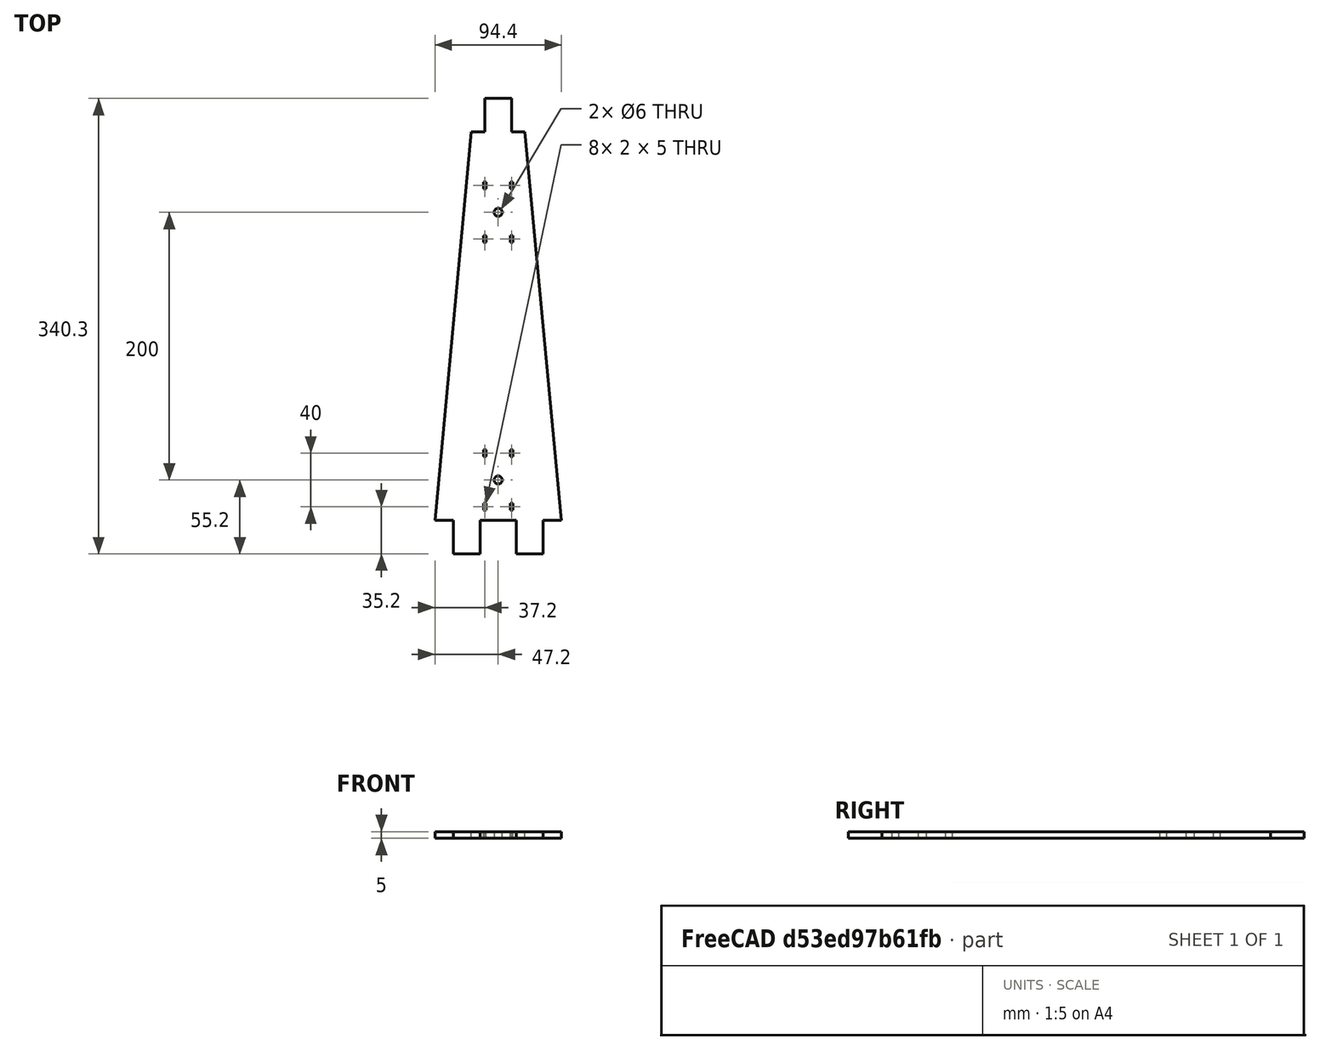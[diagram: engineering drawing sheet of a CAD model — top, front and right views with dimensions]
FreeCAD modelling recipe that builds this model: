
FCSTD DOCUMENT  (FreeCAD 0.16R6712 (Git))
Label: Vertical
License: All rights reserved
LicenseURL: http://en.wikipedia.org/wiki/All_rights_reserved
objects: Sketcher::SketchObject×1, PartDesign::Pad×1
note: 3 computed .brp shape members not serialized (recipe doc carries the construction recipe); baked Part::Feature solids carry a one-line shape summary decoded from their .brp

FEATURE [Sketcher::SketchObject] Sketch010
  sketch-geometry (67):
    g0: LineSegment StartX=-10 StartY=160.1 StartZ=0 EndX=-20 EndY=160.1 EndZ=0
    g1: LineSegment StartX=-20 StartY=160.1 StartZ=0 EndX=-47.2 EndY=-130.1 EndZ=0
    g2: LineSegment StartX=-47.2 StartY=-130.1 StartZ=0 EndX=-33.6 EndY=-130.1 EndZ=0
    g3: LineSegment StartX=-33.6 StartY=-130.1 StartZ=0 EndX=-33.6 EndY=-155.2 EndZ=0
    g4: LineSegment StartX=-33.6 StartY=-155.2 StartZ=0 EndX=-13.4 EndY=-155.2 EndZ=0
    g5: LineSegment StartX=-13.4 StartY=-155.2 StartZ=0 EndX=-13.4 EndY=-130.1 EndZ=0
    g6: LineSegment StartX=-13.4 StartY=-130.1 StartZ=0 EndX=13.4 EndY=-130.1 EndZ=0
    g7: LineSegment StartX=13.4 StartY=-130.1 StartZ=0 EndX=13.4 EndY=-155.2 EndZ=0
    g8: LineSegment StartX=13.4 StartY=-155.2 StartZ=0 EndX=33.6 EndY=-155.2 EndZ=0
    g9: LineSegment StartX=33.6 StartY=-155.2 StartZ=0 EndX=33.6 EndY=-130.1 EndZ=0
    g10: LineSegment StartX=33.6 StartY=-130.1 StartZ=0 EndX=47.2 EndY=-130.1 EndZ=0
    g11: LineSegment StartX=47.2 StartY=-130.1 StartZ=0 EndX=20 EndY=160.1 EndZ=0
    g12: LineSegment StartX=20 StartY=160.1 StartZ=0 EndX=10 EndY=160.1 EndZ=0
    g13: LineSegment StartX=10 StartY=160.1 StartZ=0 EndX=10 EndY=185.1 EndZ=0
    g14: LineSegment StartX=10 StartY=185.1 StartZ=0 EndX=-10 EndY=185.1 EndZ=0
    g15: LineSegment StartX=-10 StartY=185.1 StartZ=0 EndX=-10 EndY=160.1 EndZ=0
    g16: LineSegment [constr] StartX=-140 StartY=-130.1 StartZ=0 EndX=140 EndY=-130.1 EndZ=0
    g17: LineSegment [constr] StartX=-140 StartY=-155.2 StartZ=0 EndX=140 EndY=-155.2 EndZ=0
    g18: LineSegment [constr] StartX=-140 StartY=-100 StartZ=0 EndX=140 EndY=-100 EndZ=0
    g19: Circle CenterX=0 CenterY=-100 CenterZ=0 NormalX=0 NormalY=0 NormalZ=1 Radius=3
    g20: LineSegment [constr] StartX=-140 StartY=100 StartZ=0 EndX=140 EndY=100 EndZ=0
    g21: Circle CenterX=0 CenterY=100 CenterZ=0 NormalX=0 NormalY=0 NormalZ=1 Radius=3
    g22: LineSegment [constr] StartX=-31 StartY=19.5 StartZ=0 EndX=31 EndY=19.5 EndZ=0
    g23: LineSegment [constr] StartX=-15 StartY=-75 StartZ=0 EndX=15 EndY=-75 EndZ=0
    g24: LineSegment [constr] StartX=15 StartY=-75 StartZ=0 EndX=15 EndY=-125 EndZ=0
    g25: LineSegment [constr] StartX=15 StartY=-125 StartZ=0 EndX=-15 EndY=-125 EndZ=0
    g26: LineSegment [constr] StartX=-15 StartY=-125 StartZ=0 EndX=-15 EndY=-75 EndZ=0
    g27: LineSegment [constr] StartX=-15 StartY=125 StartZ=0 EndX=15 EndY=125 EndZ=0
    g28: LineSegment [constr] StartX=15 StartY=125 StartZ=0 EndX=15 EndY=75 EndZ=0
    g29: LineSegment [constr] StartX=15 StartY=75 StartZ=0 EndX=-15 EndY=75 EndZ=0
    g30: LineSegment [constr] StartX=-15 StartY=75 StartZ=0 EndX=-15 EndY=125 EndZ=0
    g31: LineSegment StartX=-11 StartY=-77.5 StartZ=0 EndX=-9 EndY=-77.5 EndZ=0
    g32: LineSegment StartX=-9 StartY=-77.5 StartZ=0 EndX=-9 EndY=-82.5 EndZ=0
    g33: LineSegment StartX=-9 StartY=-82.5 StartZ=0 EndX=-11 EndY=-82.5 EndZ=0
    g34: LineSegment StartX=-11 StartY=-82.5 StartZ=0 EndX=-11 EndY=-77.5 EndZ=0
    g35: LineSegment StartX=9 StartY=-77.5 StartZ=0 EndX=11 EndY=-77.5 EndZ=0
    g36: LineSegment StartX=11 StartY=-77.5 StartZ=0 EndX=11 EndY=-82.5 EndZ=0
    g37: LineSegment StartX=11 StartY=-82.5 StartZ=0 EndX=9 EndY=-82.5 EndZ=0
    g38: LineSegment StartX=9 StartY=-82.5 StartZ=0 EndX=9 EndY=-77.5 EndZ=0
    g39: LineSegment StartX=-11 StartY=-117.5 StartZ=0 EndX=-9 EndY=-117.5 EndZ=0
    g40: LineSegment StartX=-9 StartY=-117.5 StartZ=0 EndX=-9 EndY=-122.5 EndZ=0
    g41: LineSegment StartX=-9 StartY=-122.5 StartZ=0 EndX=-11 EndY=-122.5 EndZ=0
    g42: LineSegment StartX=-11 StartY=-122.5 StartZ=0 EndX=-11 EndY=-117.5 EndZ=0
    g43: LineSegment StartX=9 StartY=-117.5 StartZ=0 EndX=11 EndY=-117.5 EndZ=0
    g44: LineSegment StartX=11 StartY=-117.5 StartZ=0 EndX=11 EndY=-122.5 EndZ=0
    g45: LineSegment StartX=11 StartY=-122.5 StartZ=0 EndX=9 EndY=-122.5 EndZ=0
    g46: LineSegment StartX=9 StartY=-122.5 StartZ=0 EndX=9 EndY=-117.5 EndZ=0
    g47: LineSegment [constr] StartX=-10 StartY=-130.1 StartZ=0 EndX=-10 EndY=185.1 EndZ=0
    g48: LineSegment [constr] StartX=10 StartY=185.1 StartZ=0 EndX=10 EndY=-130.1 EndZ=0
    g49: LineSegment StartX=-11 StartY=122.5 StartZ=0 EndX=-9 EndY=122.5 EndZ=0
    g50: LineSegment StartX=-9 StartY=122.5 StartZ=0 EndX=-9 EndY=117.5 EndZ=0
    g51: LineSegment StartX=-9 StartY=117.5 StartZ=0 EndX=-11 EndY=117.5 EndZ=0
    g52: LineSegment StartX=-11 StartY=117.5 StartZ=0 EndX=-11 EndY=122.5 EndZ=0
    g53: LineSegment StartX=9 StartY=122.5 StartZ=0 EndX=11 EndY=122.5 EndZ=0
    g54: LineSegment StartX=11 StartY=122.5 StartZ=0 EndX=11 EndY=117.5 EndZ=0
    g55: LineSegment StartX=11 StartY=117.5 StartZ=0 EndX=9 EndY=117.5 EndZ=0
    g56: LineSegment StartX=9 StartY=117.5 StartZ=0 EndX=9 EndY=122.5 EndZ=0
    g57: LineSegment StartX=-11 StartY=82.5 StartZ=0 EndX=-9 EndY=82.5 EndZ=0
    g58: LineSegment StartX=-9 StartY=82.5 StartZ=0 EndX=-9 EndY=77.5 EndZ=0
    g59: LineSegment StartX=-9 StartY=77.5 StartZ=0 EndX=-11 EndY=77.5 EndZ=0
    g60: LineSegment StartX=-11 StartY=77.5 StartZ=0 EndX=-11 EndY=82.5 EndZ=0
    g61: LineSegment StartX=9 StartY=82.5 StartZ=0 EndX=11 EndY=82.5 EndZ=0
    g62: LineSegment StartX=11 StartY=82.5 StartZ=0 EndX=11 EndY=77.5 EndZ=0
    g63: LineSegment StartX=11 StartY=77.5 StartZ=0 EndX=9 EndY=77.5 EndZ=0
    g64: LineSegment StartX=9 StartY=77.5 StartZ=0 EndX=9 EndY=82.5 EndZ=0
    g65: LineSegment [constr] StartX=-15 StartY=120 StartZ=0 EndX=15 EndY=120 EndZ=0
    g66: LineSegment [constr] StartX=-15 StartY=-80 StartZ=0 EndX=15 EndY=-80 EndZ=0
  constraints (201):
    c: Horizontal(g0)
    c: Coincident(g0,g1)
    c: Coincident(g1,g2)
    c: Coincident(g2,g3)
    c: Vertical(g3)
    c: Coincident(g3,g4)
    c: Horizontal(g4)
    c: Coincident(g4,g5)
    c: Vertical(g5)
    c: Coincident(g5,g6)
    c: Horizontal(g6)
    c: Coincident(g6,g7)
    c: Vertical(g7)
    c: Coincident(g7,g8)
    c: Horizontal(g8)
    c: Coincident(g8,g9)
    c: Vertical(g9)
    c: Coincident(g9,g10)
    c: Horizontal(g10)
    c: Coincident(g10,g11)
    c: Coincident(g11,g12)
    c: Horizontal(g12)
    c: Coincident(g12,g13)
    c: Vertical(g13)
    c: Coincident(g13,g14)
    c: Horizontal(g14)
    c: Coincident(g14,g15)
    c: Coincident(g15,g0)
    c: Symmetric(g12,g0,g-2)
    c: Vertical(g15)
    c: Symmetric(g11,g0,g-2)
    c: DistanceX(g16) = 140
    c: DistanceY(g16) = -130.1
    c: Symmetric(g16,g16,g-2)
    c: Symmetric(g6,g5,g-2)
    c: Symmetric(g9,g2,g-2)
    c: Symmetric(g10,g1,g-2)
    c: Symmetric(g7,g4,g-2)
    c: Horizontal(g17)
    c: DistanceX(g16,g17) = 0
    c: DistanceY(g17,g16) = 25.1
    c: Symmetric(g17,g17,g-2)
    c: PointOnObject(g4,g17)
    c: DistanceY(g11) = 160.1
    c: DistanceY(g13,g13) = 25
    c: DistanceX(g14,g14) = 20
    c: DistanceX(g0,g0) = 10
    c: PointOnObject(g1,g16)
    c: PointOnObject(g5,g16)
    c: DistanceX(g6,g6) = 26.8
    c: DistanceX(g8,g8) = 20.2
    c: DistanceX(g10,g10) = 13.6
    c: DistanceX(g18,g16) = 0
    c: Symmetric(g18,g18,g-2)
    c: PointOnObject(g19,g18)
    c: PointOnObject(g19,g-2)
    c: Radius(g19) = 3
    c: DistanceX(g20,g16) = 0
    c: Symmetric(g20,g20,g-2)
    c: DistanceY(g-1,g20) = 100
    c: PointOnObject(g21,g20)
    c: PointOnObject(g21,g-2)
    c: Radius(g21) = 3
    c: DistanceX(g4,g4) = 20.2
    c: DistanceY(g19) = -100
    c: Horizontal(g22)
    c: DistanceX(g22,g22) = 62
    c: Symmetric(g22,g22,g-2)
    c: DistanceY(g22,g21) = 80.5
    c: Coincident(g23,g24)
    c: Coincident(g24,g25)
    c: Coincident(g25,g26)
    c: Coincident(g26,g23)
    c: Horizontal(g23)
    c: Horizontal(g25)
    c: Vertical(g24)
    c: Vertical(g26)
    c: DistanceY(g26,g26) = 50
    c: DistanceX(g23,g23) = 30
    c: Symmetric(g23,g23,g-2)
    c: Symmetric(g25,g23,g18)
    c: Coincident(g27,g28)
    c: Coincident(g28,g29)
    c: Coincident(g29,g30)
    c: Coincident(g30,g27)
    c: Horizontal(g27)
    c: Horizontal(g29)
    c: Vertical(g28)
    c: Vertical(g30)
    c: DistanceY(g30,g30) = 50
    c: DistanceX(g27,g27) = 30
    c: Symmetric(g27,g27,g-2)
    c: Symmetric(g27,g29,g20)
    c: Coincident(g31,g32)
    c: Coincident(g32,g33)
    c: Coincident(g33,g34)
    c: Coincident(g34,g31)
    c: Horizontal(g31)
    c: Horizontal(g33)
    c: Vertical(g32)
    c: Vertical(g34)
    c: Coincident(g35,g36)
    c: Coincident(g36,g37)
    c: Coincident(g37,g38)
    c: Coincident(g38,g35)
    c: Horizontal(g35)
    c: Horizontal(g37)
    c: Vertical(g36)
    c: Vertical(g38)
    c: Coincident(g39,g40)
    c: Coincident(g40,g41)
    c: Coincident(g41,g42)
    c: Coincident(g42,g39)
    c: Horizontal(g39)
    c: Horizontal(g41)
    c: Vertical(g40)
    c: Vertical(g42)
    c: Coincident(g43,g44)
    c: Coincident(g44,g45)
    c: Coincident(g45,g46)
    c: Coincident(g46,g43)
    c: Horizontal(g43)
    c: Horizontal(g45)
    c: Vertical(g44)
    c: Vertical(g46)
    c: PointOnObject(g47,g6)
    c: PointOnObject(g47,g14)
    c: Vertical(g47)
    c: PointOnObject(g48,g14)
    c: PointOnObject(g48,g6)
    c: Vertical(g48)
    c: Symmetric(g47,g48,g-2)
    c: DistanceX(g47,g48) = 20
    c: Coincident(g49,g50)
    c: Coincident(g50,g51)
    c: Coincident(g51,g52)
    c: Coincident(g52,g49)
    c: Horizontal(g49)
    c: Horizontal(g51)
    c: Vertical(g50)
    c: Vertical(g52)
    c: Coincident(g53,g54)
    c: Coincident(g54,g55)
    c: Coincident(g55,g56)
    c: Coincident(g56,g53)
    c: Horizontal(g53)
    c: Horizontal(g55)
    c: Vertical(g54)
    c: Vertical(g56)
    c: Coincident(g57,g58)
    c: Coincident(g58,g59)
    c: Coincident(g59,g60)
    c: Coincident(g60,g57)
    c: Horizontal(g57)
    c: Horizontal(g59)
    c: Vertical(g58)
    c: Vertical(g60)
    c: Coincident(g61,g62)
    c: Coincident(g62,g63)
    c: Coincident(g63,g64)
    c: Coincident(g64,g61)
    c: Horizontal(g61)
    c: Horizontal(g63)
    c: Vertical(g62)
    c: Vertical(g64)
    c: Symmetric(g49,g53,g-2)
    c: Symmetric(g49,g49,g47)
    c: Symmetric(g53,g53,g48)
    c: PointOnObject(g65,g30)
    c: PointOnObject(g65,g28)
    c: Symmetric(g50,g49,g65)
    c: Symmetric(g55,g53,g65)
    c: DistanceY(g21,g65) = 20
    c: DistanceY(g52,g52) = 5
    c: DistanceX(g49,g49) = 2
    c: Symmetric(g57,g50,g20)
    c: Symmetric(g57,g57,g47)
    c: Symmetric(g57,g61,g-2)
    c: Symmetric(g61,g61,g48)
    c: Equal(g60,g52)
    c: Equal(g64,g60)
    c: Equal(g31,g35)
    c: Equal(g35,g39)
    c: Equal(g39,g43)
    c: Equal(g43,g59)
    c: Symmetric(g39,g39,g47)
    c: Symmetric(g43,g43,g48)
    c: Symmetric(g31,g31,g47)
    c: Symmetric(g35,g35,g48)
    c: Equal(g34,g42)
    c: Equal(g42,g38)
    c: Equal(g38,g46)
    c: Equal(g46,g60)
    c: Symmetric(g31,g35,g-2)
    c: Symmetric(g43,g39,g-2)
    c: PointOnObject(g66,g26)
    c: PointOnObject(g66,g24)
    c: Horizontal(g66)
    c: Symmetric(g36,g35,g66)
    c: DistanceY(g19,g66) = 20
    c: Symmetric(g39,g32,g18)
FEATURE [PartDesign::Pad] Pad010  label="Vertical_A"
  Length = 5
  Length2 = 100
  Sketch = -> Sketch010
  Type = 0
